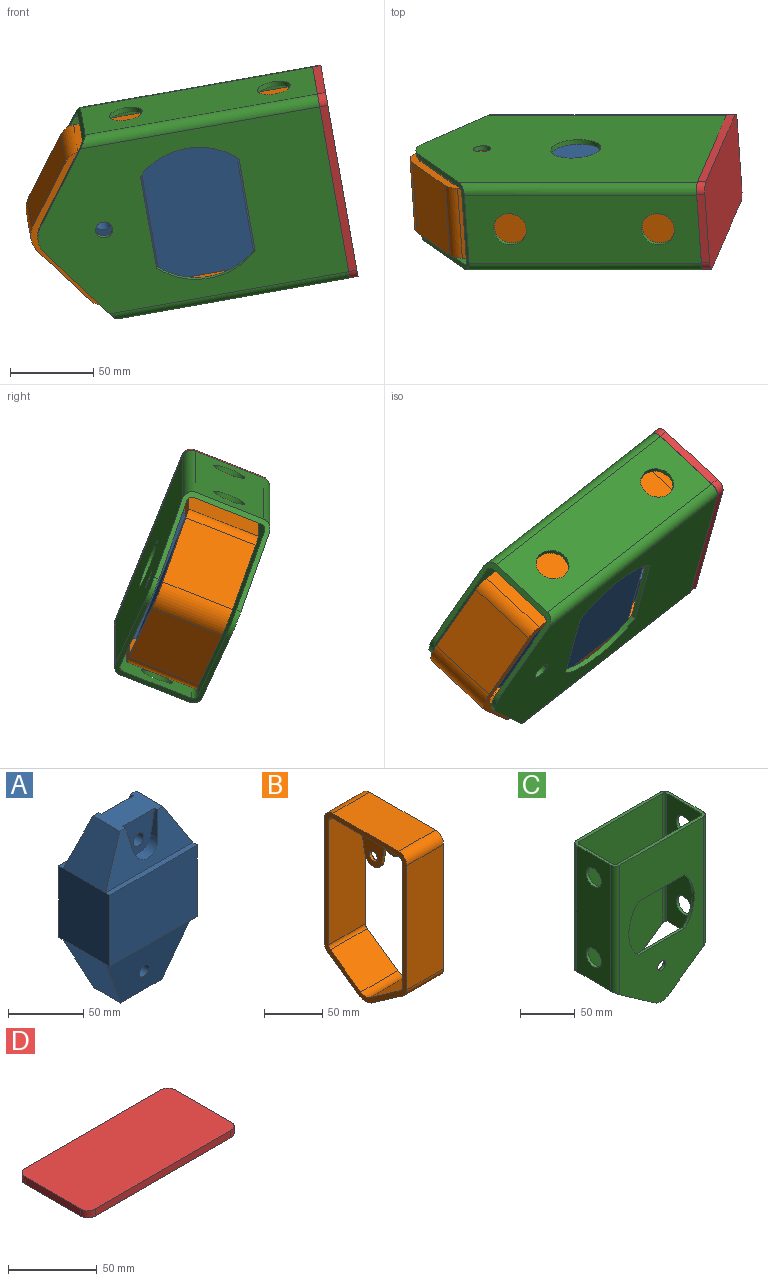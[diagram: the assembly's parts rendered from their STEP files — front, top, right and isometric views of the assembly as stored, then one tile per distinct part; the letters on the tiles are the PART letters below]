
ASSEMBLY  parts=4 mates=3
PART A: 28 faces, bbox 82.3x48.3x140.3 mm
  f0: cylinder r=5mm len=20mm, axis (0,1,0), area 628.3mm2, adj f20,f24
  f1: plane 82x36mm, normal (0,0.98,0.2), area 1559.4mm2, adj f2,f10,f15,f17,f21,f22,f23
  f2: plane 40.43x25mm, normal (0,0,1), area 862.5mm2, adj f1,f6,f15,f17,f20,f21,f22,f24
  f3: plane 82.34x46.34mm, normal (0,-0.99,-0.16), area 2742.5mm2, adj f4,f13,f16,f18,f19
  f4: plane 39.1x25mm, normal (0,0,-1), area 977.5mm2, adj f3,f5,f16,f18
  f5: plane 82x46mm, normal (0,0.99,-0.16), area 2742.5mm2, adj f4,f8,f16,f18,f19
  f6: plane 82x36mm, normal (0,-0.98,0.2), area 1559.4mm2, adj f2,f11,f15,f17,f25,f26,f27
  f7: plane 58x48mm, normal (-1,0,0), area 2784mm2, adj f8,f9,f10,f11,f12,f13,f15,f16
  f8: plane 82x4mm, normal (0,0,-1), area 328mm2, adj f5,f7,f9,f14
  f9: plane 82x58mm, normal (0,1,0), area 4756mm2, adj f7,f8,f10,f14
  f10: plane 82x4mm, normal (0,0,1), area 328mm2, adj f1,f7,f9,f14
  f11: plane 82x4mm, normal (0,0,1), area 328mm2, adj f6,f7,f12,f14
  f12: plane 82x58mm, normal (0,-1,0), area 4756mm2, adj f7,f11,f13,f14
  f13: plane 82x4mm, normal (0,0,-1), area 328mm2, adj f3,f7,f12,f14
  f14: plane 58x48mm, normal (1,0,0), area 2784mm2, adj f8,f9,f10,f11,f12,f13,f17,f18
  f15: plane 40x36mm, normal (-0.87,0,0.5), area 1351mm2, adj f1,f2,f6,f7
  f16: plane 46x40mm, normal (-0.91,0,-0.42), area 1649.5mm2, adj f3,f4,f5,f7
  f17: plane 40x36mm, normal (0.87,0,0.5), area 1351mm2, adj f1,f2,f6,f14
  f18: plane 46x40mm, normal (0.91,0,-0.42), area 1649.5mm2, adj f3,f4,f5,f14
  f19: cylinder r=5mm len=32.5mm, axis (0,1,0), area 969.8mm2, adj f3,f5
  f20: plane 29.65x29.2mm, normal (0,1,0), area 598.6mm2, adj f0,f2,f21,f22,f23
  f21: plane 19.71x6.61mm, normal (0.98,0,0.17), area 91.2mm2, adj f1,f2,f20,f23
  f22: plane 19.71x6.61mm, normal (-0.98,0,0.17), area 91.2mm2, adj f1,f2,f20,f23
  f23: cylinder r=11.5mm len=22.65mm, axis (0,1,0), area 252.8mm2, adj f1,f20,f21,f22
  f24: plane 29.65x29.2mm, normal (0,-1,0), area 598.6mm2, adj f0,f2,f25,f26,f27
  f25: cylinder r=11.5mm len=22.65mm, axis (0,-1,0), area 252.8mm2, adj f6,f24,f26,f27
  f26: plane 19.71x6.61mm, normal (0.98,0,0.17), area 91.2mm2, adj f2,f6,f24,f25
  f27: plane 19.71x6.61mm, normal (-0.98,0,0.17), area 91.2mm2, adj f2,f6,f24,f25
PART B: 34 faces, bbox 45x100x178 mm
  f0: plane 28.51x5.1mm, normal (0,-0.98,-0.18), area 86.9mm2, adj f2,f8,f28,f32
  f1: plane 28.51x5.1mm, normal (0,-0.98,-0.18), area 86.9mm2, adj f3,f8,f29,f31
  f2: cylinder r=10.5mm len=20.24mm, axis (-1,0,0), area 82.8mm2, adj f0,f4,f28,f32
  f3: cylinder r=10.5mm len=20.24mm, axis (-1,0,0), area 82.8mm2, adj f1,f5,f29,f31
  f4: plane 26.8x4.66mm, normal (0,0.99,-0.17), area 81.6mm2, adj f2,f8,f28,f32
  f5: plane 26.8x4.66mm, normal (0,0.99,-0.17), area 81.6mm2, adj f3,f8,f29,f31
  f6: plane 178x100mm, normal (1,0,0), area 2430.4mm2, adj f8,f9,f10,f11,f12,f13,f14,f15
  f7: plane 178x100mm, normal (-1,0,0), area 2430.4mm2, adj f8,f9,f10,f11,f12,f13,f14,f15
  f8: plane 80x45mm, normal (0,0,-1), area 3420mm2, adj f0,f1,f4,f5,f6,f7,f9,f26
  f9: cylinder r=5mm len=45mm, axis (-1,0,0), area 353.4mm2, adj f6,f7,f8,f10
  f10: plane 131.1x45mm, normal (0,-1,0), area 5899.3mm2, adj f6,f7,f9,f11
  f11: cylinder r=5mm len=45mm, axis (-1,0,0), area 216mm2, adj f6,f7,f10,f12
  f12: plane 45x37.13mm, normal (0,-0.57,0.82), area 2039.8mm2, adj f6,f7,f11,f13
  f13: cylinder r=10mm len=45mm, axis (-1,0,0), area 549.8mm2, adj f6,f7,f12,f14
  f14: plane 45x37.13mm, normal (0,0.57,0.82), area 2039.8mm2, adj f6,f7,f13,f15
  f15: cylinder r=5mm len=45mm, axis (-1,0,0), area 216mm2, adj f6,f7,f14,f16
  f16: plane 131.1x45mm, normal (0,1,0), area 5899.3mm2, adj f6,f7,f15,f26
  f17: plane 80x45mm, normal (0,0,1), area 3600mm2, adj f6,f7,f18,f27
  f18: cylinder r=10mm len=45mm, axis (-1,0,0), area 706.9mm2, adj f6,f7,f17,f19
  f19: plane 131.1x45mm, normal (0,-1,0), area 5899.3mm2, adj f6,f7,f18,f20
  f20: cylinder r=10mm len=45mm, axis (-1,0,0), area 432mm2, adj f6,f7,f19,f21
  f21: plane 45x37.13mm, normal (0,-0.57,-0.82), area 2039.8mm2, adj f6,f7,f20,f22
  f22: cylinder r=15mm len=45mm, axis (-1,0,0), area 824.7mm2, adj f6,f7,f21,f23
  f23: plane 45x37.13mm, normal (0,0.57,-0.82), area 2039.8mm2, adj f6,f7,f22,f24
  f24: cylinder r=10mm len=45mm, axis (-1,0,0), area 432mm2, adj f6,f7,f23,f25
  f25: plane 131.1x45mm, normal (0,1,0), area 5899.3mm2, adj f6,f7,f24,f27
  f26: cylinder r=5mm len=45mm, axis (-1,0,0), area 353.4mm2, adj f6,f7,f8,f16
  f27: cylinder r=10mm len=45mm, axis (-1,0,0), area 706.9mm2, adj f6,f7,f17,f25
  f28: plane 35.5x30mm, normal (-1,0,0), area 734.2mm2, adj f0,f2,f4,f8,f30
  f29: plane 35.5x30mm, normal (1,0,0), area 734.2mm2, adj f1,f3,f5,f8,f33
  f30: cylinder r=5mm len=10mm, axis (-1,0,0), area 94.2mm2, adj f28,f32
  f31: plane 35.5x30mm, normal (-1,0,0), area 734.2mm2, adj f1,f3,f5,f8,f33
  f32: plane 35.5x30mm, normal (1,0,0), area 734.2mm2, adj f0,f2,f4,f8,f30
  f33: cylinder r=5mm len=10mm, axis (-1,0,0), area 94.2mm2, adj f29,f31
PART C: 32 faces, bbox 120x56x180 mm
  f0: plane 180x108mm, normal (0,-1,0), area 13016.8mm2, adj f2,f3,f4,f8,f9,f19,f20,f21
  f1: plane 180x108mm, normal (0,1,0), area 13016.8mm2, adj f2,f3,f4,f8,f9,f12,f16,f19
  f2: plane 56x51.4mm, normal (-0.57,0,-0.82), area 545.4mm2, adj f0,f1,f3,f6,f10,f11,f15,f16
  f3: cylinder r=15mm len=17.21mm, axis (0,1,0), area 55mm2, adj f0,f1,f2,f4
  f4: plane 56x51.4mm, normal (0.57,0,-0.82), area 545.4mm2, adj f0,f1,f3,f6,f7,f11,f12,f13
  f5: cylinder r=5.1mm len=10.2mm, axis (0,1,0), area 96.1mm2, adj f11,f15
  f6: cylinder r=15mm len=17.21mm, axis (0,1,0), area 55mm2, adj f2,f4,f11,f15
  f7: plane 141.3x44mm, normal (1,0,0), area 5588.8mm2, adj f4,f8,f26,f27,f28,f30
  f8: plane 120x56mm, normal (0,0,1), area 996.8mm2, adj f0,f1,f7,f10,f11,f12,f13,f14
  f9: cylinder r=5.1mm len=10.2mm, axis (0,1,0), area 96.1mm2, adj f0,f1
  f10: plane 141.3x44mm, normal (-1,0,0), area 5588.8mm2, adj f2,f8,f24,f25,f29,f31
  f11: plane 180x108mm, normal (0,1,0), area 16947.2mm2, adj f2,f4,f5,f6,f8,f23,f28,f29
  f12: cylinder r=3mm len=145.5mm, axis (0,0,1), area 679.4mm2, adj f1,f4,f8,f13
  f13: plane 143.4x44mm, normal (-1,0,0), area 5681.3mm2, adj f4,f8,f12,f14,f26,f27
  f14: cylinder r=3mm len=145.5mm, axis (0,0,1), area 679.4mm2, adj f4,f8,f13,f15
  f15: plane 180x108mm, normal (0,-1,0), area 16947.2mm2, adj f2,f4,f5,f6,f8,f14,f17,f23
  f16: cylinder r=3mm len=145.5mm, axis (0,0,1), area 679.4mm2, adj f1,f2,f8,f18
  f17: cylinder r=3mm len=145.5mm, axis (0,0,1), area 679.4mm2, adj f2,f8,f15,f18
  f18: plane 143.4x44mm, normal (1,0,0), area 5681.3mm2, adj f2,f8,f16,f17,f24,f25
  f19: plane 60.21x3mm, normal (0,0,1), area 180.6mm2, adj f0,f1,f20,f22
  f20: cylinder r=42.5mm len=60mm, axis (0,-1,0), area 199.8mm2, adj f0,f1,f19,f21
  f21: plane 60.21x3mm, normal (0,0,-1), area 180.6mm2, adj f0,f1,f20,f22
  f22: cylinder r=42.5mm len=60mm, axis (0,-1,0), area 199.8mm2, adj f0,f1,f19,f21
  f23: cylinder r=15mm len=30mm, axis (0,-1,0), area 282.7mm2, adj f11,f15
  f24: cylinder r=10mm len=20mm, axis (1,0,0), area 188.5mm2, adj f10,f18
  f25: cylinder r=10mm len=20mm, axis (1,0,0), area 188.5mm2, adj f10,f18
  f26: cylinder r=10mm len=20mm, axis (1,0,0), area 188.5mm2, adj f7,f13
  f27: cylinder r=10mm len=20mm, axis (1,0,0), area 188.5mm2, adj f7,f13
  f28: cylinder r=6mm len=145.5mm, axis (0,0,1), area 1346.1mm2, adj f4,f7,f8,f11
  f29: cylinder r=6mm len=145.5mm, axis (0,0,-1), area 1346.1mm2, adj f2,f8,f10,f11
  f30: cylinder r=6mm len=145.5mm, axis (0,0,-1), area 1346.1mm2, adj f0,f4,f7,f8
  f31: cylinder r=6mm len=145.5mm, axis (0,0,1), area 1346.1mm2, adj f0,f2,f8,f10
PART D: 10 faces, bbox 120x56x5 mm
  f0: cylinder r=6mm len=6mm, axis (0,0,-1), area 47.1mm2, adj f1,f7,f8,f9
  f1: plane 108x5mm, normal (0,-1,0), area 540mm2, adj f0,f2,f8,f9
  f2: cylinder r=6mm len=6mm, axis (0,0,-1), area 47.1mm2, adj f1,f3,f8,f9
  f3: plane 44x5mm, normal (1,0,0), area 220mm2, adj f2,f4,f8,f9
  f4: cylinder r=6mm len=6mm, axis (0,0,-1), area 47.1mm2, adj f3,f5,f8,f9
  f5: plane 108x5mm, normal (0,1,0), area 540mm2, adj f4,f6,f8,f9
  f6: cylinder r=6mm len=6mm, axis (0,0,-1), area 47.1mm2, adj f5,f7,f8,f9
  f7: plane 44x5mm, normal (-1,0,0), area 220mm2, adj f0,f6,f8,f9
  f8: plane 120x56mm, normal (0,0,1), area 6689.1mm2, adj f0,f1,f2,f3,f4,f5,f6,f7
  f9: plane 120x56mm, normal (0,0,-1), area 6689.1mm2, adj f0,f1,f2,f3,f4,f5,f6,f7
PLACE A rot(axis=(0.18,0.96,0.22),82.4deg) t=(27.51,-41.71,84.92)mm
PLACE B rot(axis=(-0.47,0.69,-0.56),101.3deg) t=(-53,-5.7,40.76)mm
PLACE C rot(axis=(0.18,0.96,0.22),82.4deg) t=(15.58,-0.45,54.72)mm
PLACE D rot(axis=(0.18,0.96,0.22),82.4deg) t=(116.39,-27.12,58.87)mm
MATE cylindrical B.f2 <-> A.f0  axis (0.06,-0.93,-0.37) through (79.77,-17.22,59.24)mm
MATE planar D.f9 <-> C.f8  axis (-0.98,0,-0.17) through (115.85,-26.09,61.9)mm
MATE cylindrical A.f19 <-> C.f5  axis (-0.06,0.93,0.37) through (-20.95,-41.78,31.52)mm
